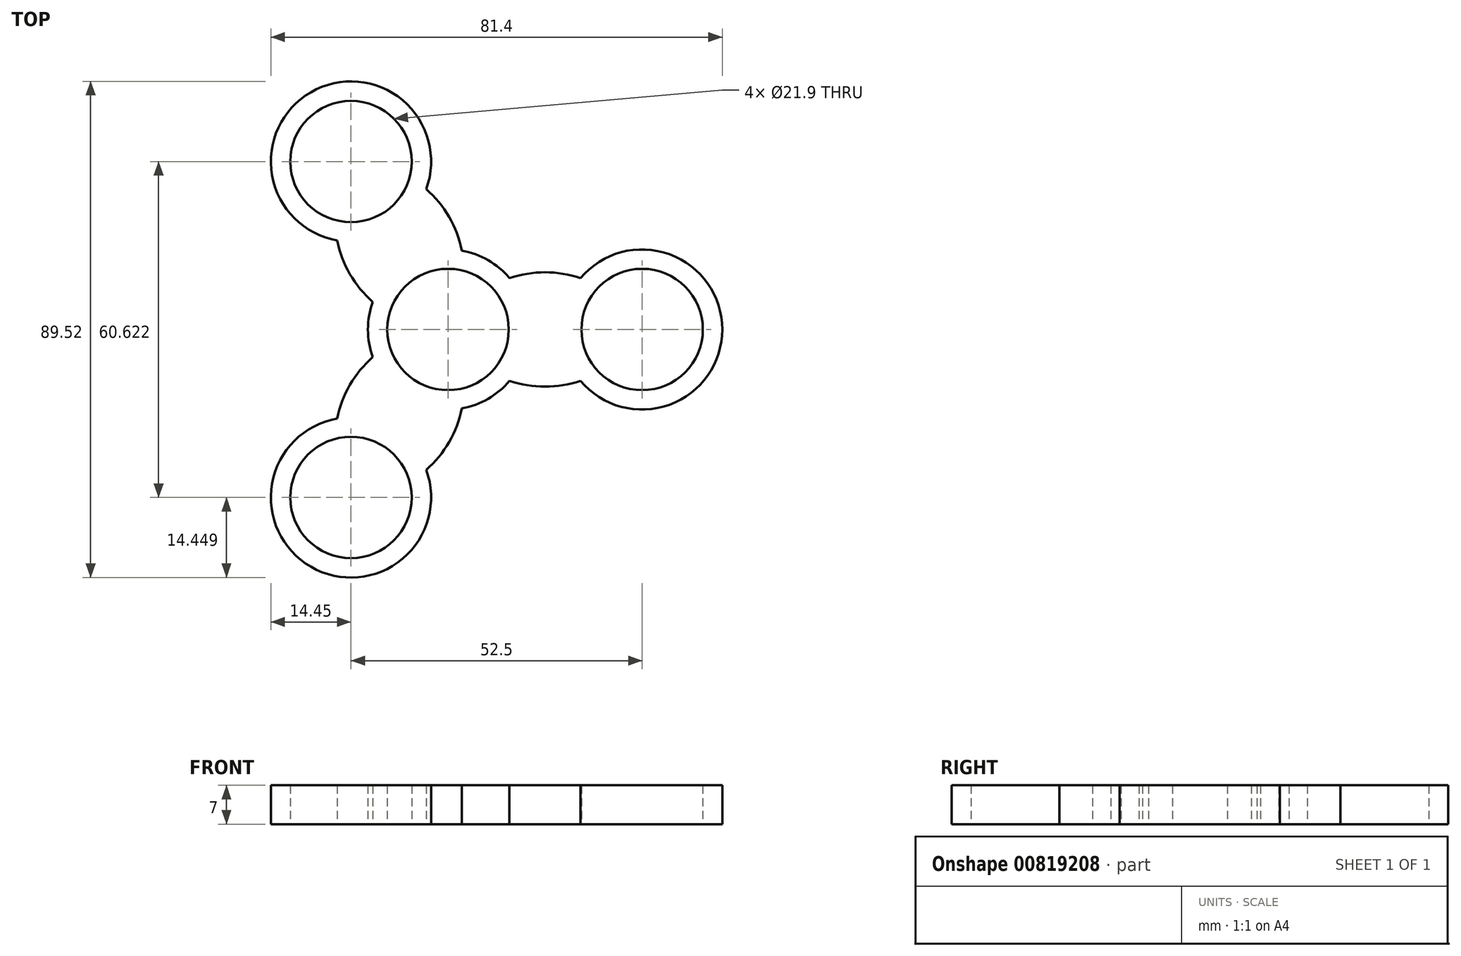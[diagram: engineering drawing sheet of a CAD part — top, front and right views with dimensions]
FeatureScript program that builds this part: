
annotation { "Feature Type Name" : "Feature", "Feature Type Description" : "" }
export const myFeature = defineFeature(function(context is Context, id is Id, definition is map)
    precondition{}
    {
        {
            var Q0;
            Q0=qCreatedBy(makeId("Top.planeOp"),FACE);
            var sketch = newSketch(context, id + "F0", { "sketchPlane" : qUnion([Q0])});
            skCircle(sketch, "E0", {"center": v(0, 0) * mm, "radius": 10.95 * mm});
            skCircle(sketch, "E1.0", {"center": v(0, 0) * mm, "radius": 14.45 * mm});
            skLineSegment(sketch, "E2", {"start": v(0, 0) * mm, "end": v(35, 0) * mm, "construction": true});
            skLineSegment(sketch, "E3", {"start": v(0, 0) * mm, "end": v(-17.5, 30.31) * mm, "construction": true});
            skLineSegment(sketch, "E4", {"start": v(0, 0) * mm, "end": v(-17.5, -30.31) * mm, "construction": true});
            skCircle(sketch, "E5", {"center": v(-17.5, 30.31) * mm, "radius": 10.95 * mm});
            skCircle(sketch, "E6", {"center": v(35, 0) * mm, "radius": 10.95 * mm});
            skCircle(sketch, "E7", {"center": v(-17.5, -30.31) * mm, "radius": 10.95 * mm});
            skCircle(sketch, "E8.0", {"center": v(-17.5, 30.31) * mm, "radius": 14.45 * mm});
            skCircle(sketch, "E9.0", {"center": v(35, 0) * mm, "radius": 14.45 * mm});
            skCircle(sketch, "E10.0", {"center": v(-17.5, -30.31) * mm, "radius": 14.45 * mm});
            skArc(sketch, "E11", {"start": v(-17.5, 30.31) * mm, "mid": v(-17.69, 10) * mm, "end": v(0, 0) * mm});
            skArc(sketch, "E12", {"start": v(0, 0) * mm, "mid": v(0.19, 20.31) * mm, "end": v(-17.5, 30.31) * mm});
            skArc(sketch, "E13", {"start": v(35, 0) * mm, "mid": v(17.5, 10.32) * mm, "end": v(0, 0) * mm});
            skArc(sketch, "E14", {"start": v(0, 0) * mm, "mid": v(17.5, -10.32) * mm, "end": v(35, 0) * mm});
            skArc(sketch, "E15", {"start": v(-17.5, -30.31) * mm, "mid": v(0.19, -20.31) * mm, "end": v(0, 0) * mm});
            skArc(sketch, "E16", {"start": v(0, 0) * mm, "mid": v(-17.69, -10) * mm, "end": v(-17.5, -30.31) * mm});
            skSolve(sketch);
        }
        {
            var Q0;
            Q0 = qSketchRegion(id + "F0", true);
            extrude(context, id + "F1", {"entities" : qUnion([Q0]), "depth" : 7 * mm, "offsetDistance" : 25 * mm});
        }
    });
